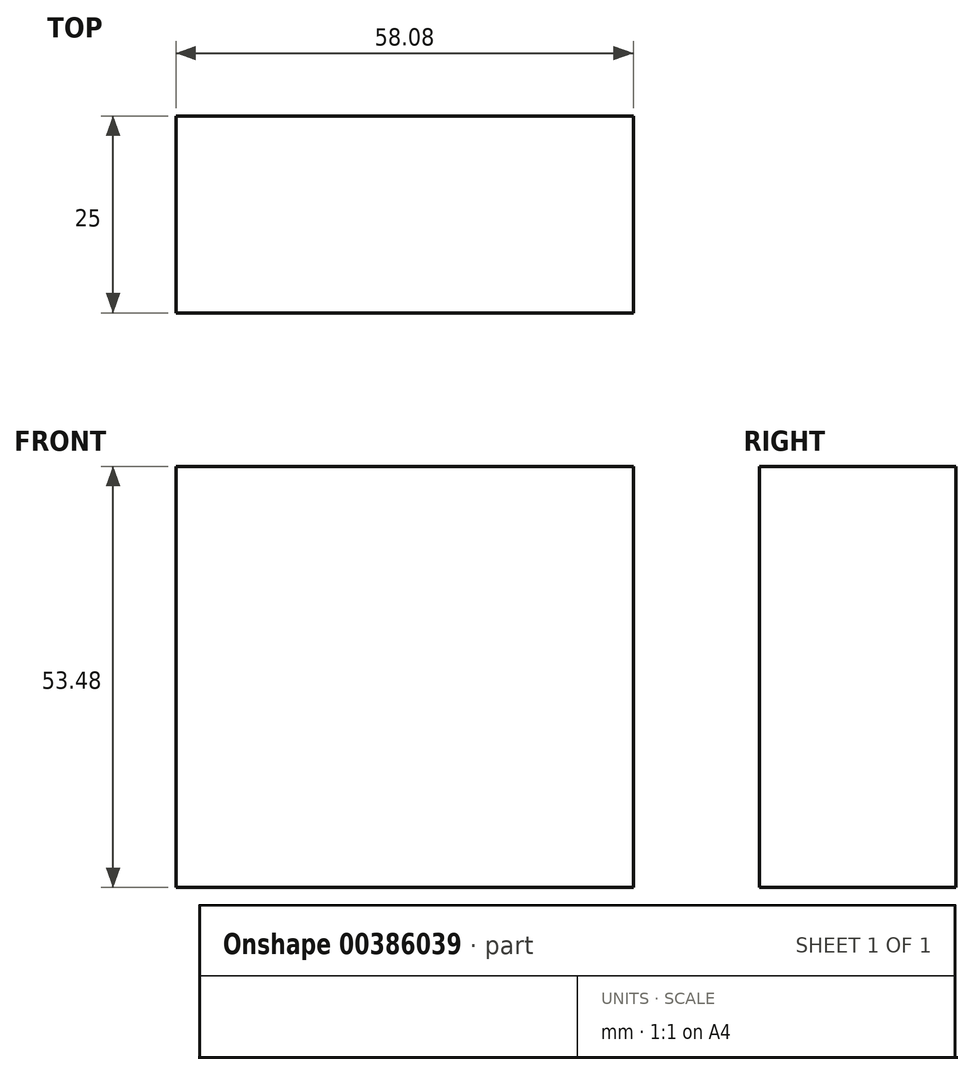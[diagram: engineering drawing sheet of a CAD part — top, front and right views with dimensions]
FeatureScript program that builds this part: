
annotation { "Feature Type Name" : "Feature", "Feature Type Description" : "" }
export const myFeature = defineFeature(function(context is Context, id is Id, definition is map)
    precondition{}
    {
        {
            var Q0;
            Q0=qCreatedBy(makeId("Front.planeOp"),FACE);
            var sketch = newSketch(context, id + "F0", { "sketchPlane" : qUnion([Q0])});
            skLineSegment(sketch, "E0.bottom", {"start": v(-75.1, 7.36) * mm, "end": v(-17.02, 7.36) * mm});
            skLineSegment(sketch, "E0.top", {"start": v(-75.1, 60.84) * mm, "end": v(-17.02, 60.84) * mm});
            skLineSegment(sketch, "E0.left", {"start": v(-75.1, 7.36) * mm, "end": v(-75.1, 60.84) * mm});
            skLineSegment(sketch, "E0.right", {"start": v(-17.02, 7.36) * mm, "end": v(-17.02, 60.84) * mm});
            skPoint(sketch, "E0.middle", {"position": v(-46.06, 34.1) * mm});
            skSolve(sketch);
        }
        {
            var Q0;
            Q0=makeQuery(id+"F0.imprint","IMPRINT",FACE,{"disambiguationData":[TD([[makeQuery(id+"F0.imprint","IMPRINT",EDGE,{"derivedFrom":sQuery(id+"F0.wireOp",EDGE,"E0.bottom")}),1.0]])]});
            extrude(context, id + "F1", {"entities" : qUnion([Q0]), "depth" : 25 * mm});
        }
    });
